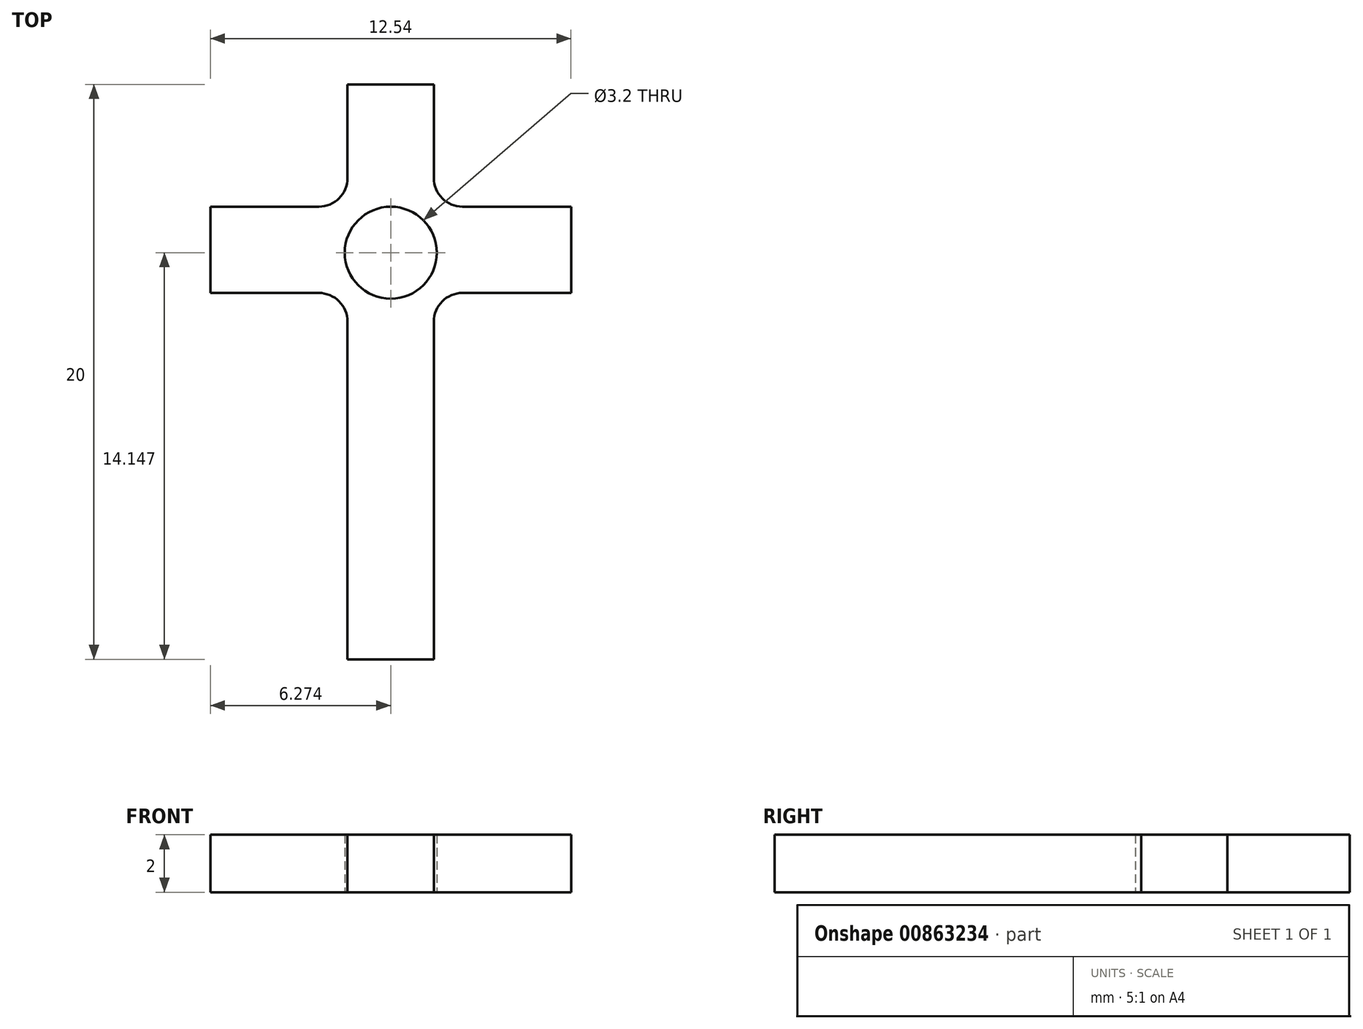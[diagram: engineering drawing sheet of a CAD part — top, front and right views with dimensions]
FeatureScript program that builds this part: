
annotation { "Feature Type Name" : "Feature", "Feature Type Description" : "" }
export const myFeature = defineFeature(function(context is Context, id is Id, definition is map)
    precondition{}
    {
        {
            var Q0;
            Q0=qCreatedBy(makeId("Top.planeOp"),FACE);
            var sketch = newSketch(context, id + "F0", { "sketchPlane" : qUnion([Q0])});
            skLineSegment(sketch, "E0.bottom", {"start": v(-56.18, 0) * mm, "end": v(-53.18, 0) * mm});
            skLineSegment(sketch, "E0.top", {"start": v(-56.18, 20) * mm, "end": v(-53.18, 20) * mm});
            skLineSegment(sketch, "E0.left", {"start": v(-56.18, 0) * mm, "end": v(-56.18, 12.75) * mm});
            skLineSegment(sketch, "E0.right", {"start": v(-53.18, 0) * mm, "end": v(-53.18, 12.75) * mm});
            skLineSegment(sketch, "E1.bottom", {"start": v(-60.95, 15.75) * mm, "end": v(-56.18, 15.75) * mm});
            skLineSegment(sketch, "E1.top", {"start": v(-60.95, 12.75) * mm, "end": v(-56.18, 12.75) * mm});
            skLineSegment(sketch, "E1.left", {"start": v(-60.95, 15.75) * mm, "end": v(-60.95, 12.75) * mm});
            skLineSegment(sketch, "E1.right", {"start": v(-48.4, 15.75) * mm, "end": v(-48.4, 12.75) * mm});
            skCircle(sketch, "E2", {"center": v(-54.68, 14.15) * mm, "radius": 1.6 * mm});
            skPoint(sketch, "E2.centerSnap0", {"position": v(-54.68, 15.75) * mm});
            skLineSegment(sketch, "E3.trimOffspring", {"start": v(-56.18, 15.75) * mm, "end": v(-56.18, 20) * mm});
            skLineSegment(sketch, "E4.trimOffspring", {"start": v(-53.18, 15.75) * mm, "end": v(-53.18, 20) * mm});
            skLineSegment(sketch, "E5.trimOffspring", {"start": v(-53.18, 15.75) * mm, "end": v(-48.4, 15.75) * mm});
            skLineSegment(sketch, "E6.trimOffspring", {"start": v(-53.18, 12.75) * mm, "end": v(-48.4, 12.75) * mm});
            skSolve(sketch);
        }
        {
            var Q0;
            Q0 = qSketchRegion(id + "F0", true);
            extrude(context, id + "F1", {"entities" : qUnion([Q0]), "depth" : 2 * mm, "offsetDistance" : 25.4 * mm});
        }
        {
            var Q0;
            Q0=makeQuery(id+"F1.opExtrude","SWEPT_EDGE",EDGE,{"disambiguationData":[OSD([sQuery(id+"F0.wireOp",EDGE,"E1.bottom"),sQuery(id+"F0.wireOp",EDGE,"E3.trimOffspring")])]});
            var Q1;
            Q1=makeQuery(id+"F1.opExtrude","SWEPT_EDGE",EDGE,{"disambiguationData":[OSD([sQuery(id+"F0.wireOp",EDGE,"E4.trimOffspring"),sQuery(id+"F0.wireOp",EDGE,"E5.trimOffspring")])]});
            var Q2;
            Q2=makeQuery(id+"F1.opExtrude","SWEPT_EDGE",EDGE,{"disambiguationData":[OSD([sQuery(id+"F0.wireOp",EDGE,"E0.left"),sQuery(id+"F0.wireOp",EDGE,"E1.top")])]});
            var Q3;
            Q3=makeQuery(id+"F1.opExtrude","SWEPT_EDGE",EDGE,{"disambiguationData":[OSD([sQuery(id+"F0.wireOp",EDGE,"E0.right"),sQuery(id+"F0.wireOp",EDGE,"E6.trimOffspring")])]});
            fillet(context, id + "F2", {"entities" : qUnion([Q0, Q1, Q2, Q3]), "radius" : 1 * mm, "allowEdgeOverflow" : false});
        }
    });
